# Revit family: Base_Cabinet-Danver-Wall_Cabinets-WSxxzz-24-1D
name_source: partatom
category: Casework
units: mm (PartAtom-declared; Revit-internal decimal feet)

## family parameters
Always vertical = Yes
Classification Number = 23.40.35.17.47
Cut with Voids When Loaded = No
Room Calculation Point = No
Shared = No
Work Plane-Based = No

## types (2) — shared parameters
Assembly Code = E2010.30
Cabinet Material = Metal - Danver - Stainless Steel
Construction Type = 304 Grade Stainless Steel
Default Elevation = 0' - 0"
Depth = 2' - 0"
Description = Single Door Wall Cabinets
Door Material = Metal - Danver - Stainless Steel
Handle Material = Metal - Danver - Chrome Plated Steel
Instruction Sheet Link = https://danver.com
Keynote = 12 31 00
Manufacturer = Danver Outdoor Kitchens
Product Documentation Link = https://danver.com
Product Name = Wall Cabinets: 24" Deep
Product Page URL = https://danver.com
URL = www.danver.com
Version = 2020 - V0.0a
Warranty URL = https://danver.com
Width = 1' - 3"

## per-type parameters (varying)
| type | Height | Model |
| 15" Width - 24" Depth - 15" Height | 1' - 3" | WS1515-24 |
| 15" Width - 24" Depth - 18" Height | 1' - 6" | WS1518-24 |

## geometry (parser evidence)
native form markers: Sweep x8
no freeform markers — native parametric forms only
